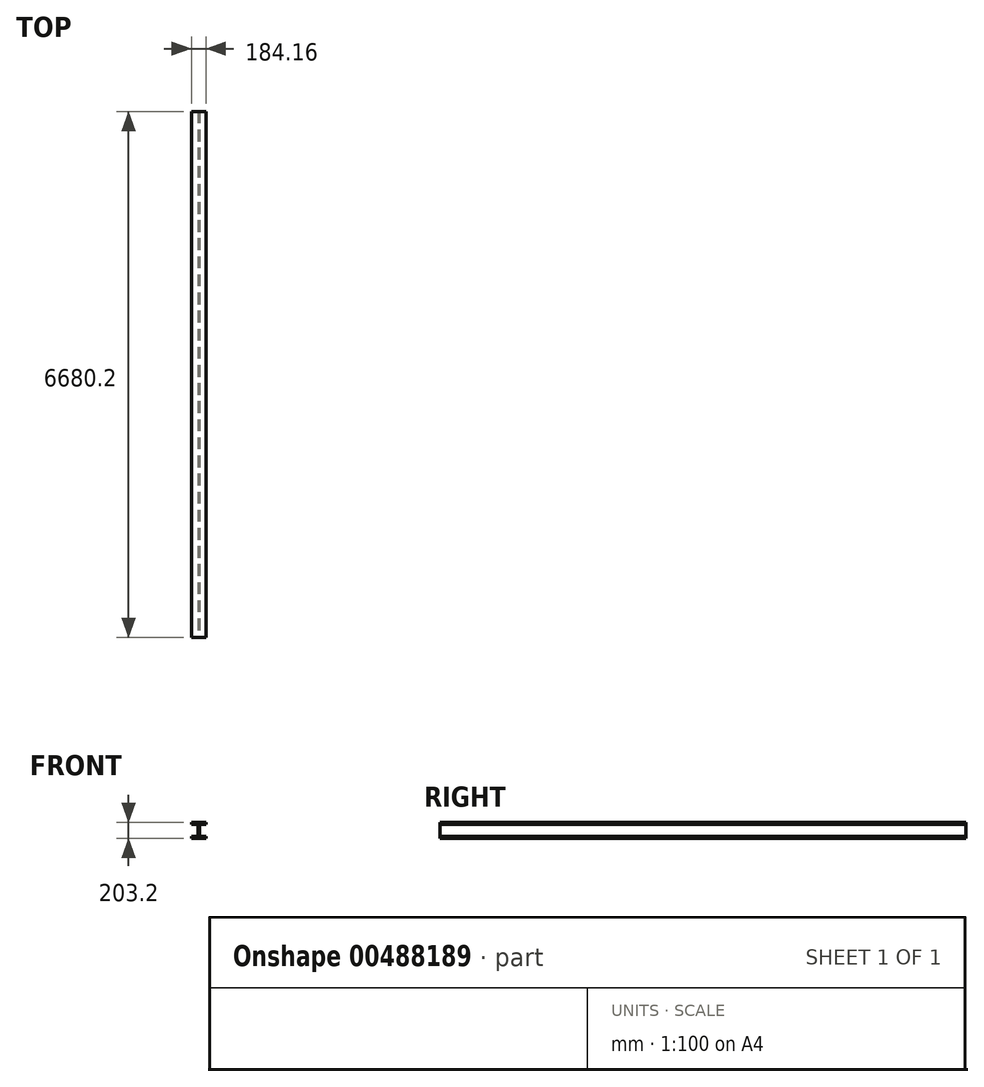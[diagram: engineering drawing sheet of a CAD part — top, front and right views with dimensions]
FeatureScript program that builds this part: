
annotation { "Feature Type Name" : "Feature", "Feature Type Description" : "" }
export const myFeature = defineFeature(function(context is Context, id is Id, definition is map)
    precondition{}
    {
        {
            var Q0;
            Q0=qCreatedBy(makeId("Front.planeOp"),FACE);
            var sketch = newSketch(context, id + "F0", { "sketchPlane" : qUnion([Q0])});
            skLineSegment(sketch, "E0", {"start": v(92.08, -76.2) * mm, "end": v(12.07, -76.2) * mm});
            skLineSegment(sketch, "E1", {"start": v(9.52, -73.66) * mm, "end": v(9.52, 73.66) * mm});
            skLineSegment(sketch, "E2", {"start": v(12.07, 76.2) * mm, "end": v(92.08, 76.2) * mm});
            skLineSegment(sketch, "E3", {"start": v(-92.08, 76.2) * mm, "end": v(-12.07, 76.2) * mm});
            skLineSegment(sketch, "E4", {"start": v(-9.53, 73.66) * mm, "end": v(-9.53, -73.66) * mm});
            skLineSegment(sketch, "E5", {"start": v(-12.06, -76.2) * mm, "end": v(-92.08, -76.2) * mm});
            skLineSegment(sketch, "E6", {"start": v(0, 0) * mm, "end": v(-9.52, 0) * mm, "construction": true});
            skLineSegment(sketch, "E7", {"start": v(0, 0) * mm, "end": v(9.52, 0) * mm, "construction": true});
            skLineSegment(sketch, "E8", {"start": v(0, 0) * mm, "end": v(0, 101.6) * mm, "construction": true});
            skLineSegment(sketch, "E9", {"start": v(0, 0) * mm, "end": v(0, -101.6) * mm, "construction": true});
            skPoint(sketch, "E10.visualSharp", {"position": v(-9.53, 76.2) * mm});
            skArc(sketch, "E10.filletArc", {"start": v(-9.52, 73.66) * mm, "mid": v(-10.27, 75.46) * mm, "end": v(-12.07, 76.2) * mm});
            skPoint(sketch, "E11.visualSharp", {"position": v(9.53, 76.2) * mm});
            skArc(sketch, "E11.filletArc", {"start": v(12.07, 76.2) * mm, "mid": v(10.27, 75.46) * mm, "end": v(9.52, 73.66) * mm});
            skPoint(sketch, "E12.visualSharp", {"position": v(9.53, -76.2) * mm});
            skArc(sketch, "E12.filletArc", {"start": v(9.52, -73.66) * mm, "mid": v(10.27, -75.46) * mm, "end": v(12.07, -76.2) * mm});
            skPoint(sketch, "E13.visualSharp", {"position": v(-9.53, -76.2) * mm});
            skArc(sketch, "E13.filletArc", {"start": v(-12.06, -76.2) * mm, "mid": v(-10.27, -75.46) * mm, "end": v(-9.52, -73.66) * mm});
            skPoint(sketch, "E14.visualSharp", {"position": v(-92.08, 101.6) * mm});
            skPoint(sketch, "E15.visualSharp", {"position": v(92.08, 101.6) * mm});
            skPoint(sketch, "E16.visualSharp", {"position": v(92.08, 76.2) * mm});
            skPoint(sketch, "E17.visualSharp", {"position": v(92.08, -101.6) * mm});
            skPoint(sketch, "E18.visualSharp", {"position": v(-92.08, -76.2) * mm});
            skPoint(sketch, "E19.visualSharp", {"position": v(-92.08, -101.6) * mm});
            skLineSegment(sketch, "E20", {"start": v(92.08, -76.2) * mm, "end": v(92.08, -101.6) * mm});
            skLineSegment(sketch, "E21", {"start": v(-92.08, -76.2) * mm, "end": v(-92.08, -101.6) * mm});
            skLineSegment(sketch, "E22", {"start": v(-92.08, 101.6) * mm, "end": v(-92.08, 76.2) * mm});
            skLineSegment(sketch, "E23", {"start": v(92.08, 101.6) * mm, "end": v(92.08, 76.2) * mm});
            skLineSegment(sketch, "E24", {"start": v(-92.08, 101.6) * mm, "end": v(92.08, 101.6) * mm});
            skLineSegment(sketch, "E25", {"start": v(-92.07, -101.6) * mm, "end": v(92.08, -101.6) * mm});
            skSolve(sketch);
        }
        {
            var Q0;
            Q0=makeQuery(id+"F0.imprint","IMPRINT",FACE,{"disambiguationData":[TD([[makeQuery(id+"F0.imprint","IMPRINT",EDGE,{"derivedFrom":sQuery(id+"F0.wireOp",EDGE,"E0")}),1.0]])]});
            extrude(context, id + "F1", {"entities" : qUnion([Q0]), "oppositeDirection" : true, "depth" : 6680.2 * mm, "offsetDistance" : 25.4 * mm});
        }
    });
